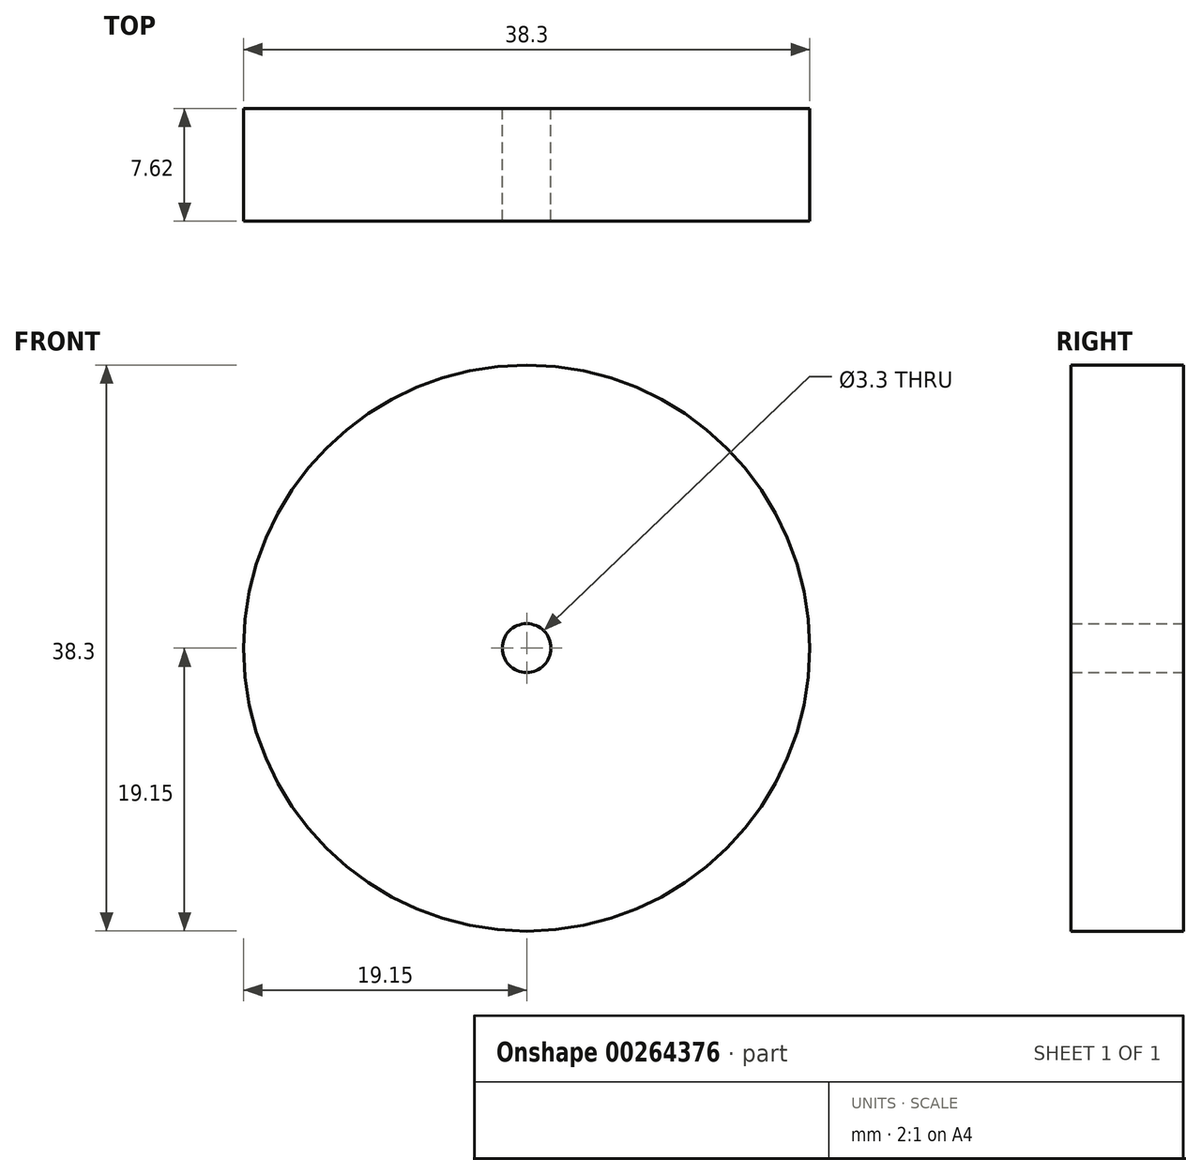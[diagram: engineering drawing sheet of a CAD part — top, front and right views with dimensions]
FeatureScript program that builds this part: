
annotation { "Feature Type Name" : "Feature", "Feature Type Description" : "" }
export const myFeature = defineFeature(function(context is Context, id is Id, definition is map)
    precondition{}
    {
        {
            var Q0;
            Q0=qCreatedBy(makeId("Front.planeOp"),FACE);
            var sketch = newSketch(context, id + "F0", { "sketchPlane" : qUnion([Q0])});
            skCircle(sketch, "E0", {"center": v(0, 0) * mm, "radius": 19.15 * mm});
            skCircle(sketch, "E1", {"center": v(0, 0) * mm, "radius": 1.65 * mm});
            skSolve(sketch);
        }
        {
            var Q0;
            Q0 = qSketchRegion(id + "F0", true);
            extrude(context, id + "F1", {"entities" : qUnion([Q0]), "depth" : 7.62 * mm});
        }
    });
